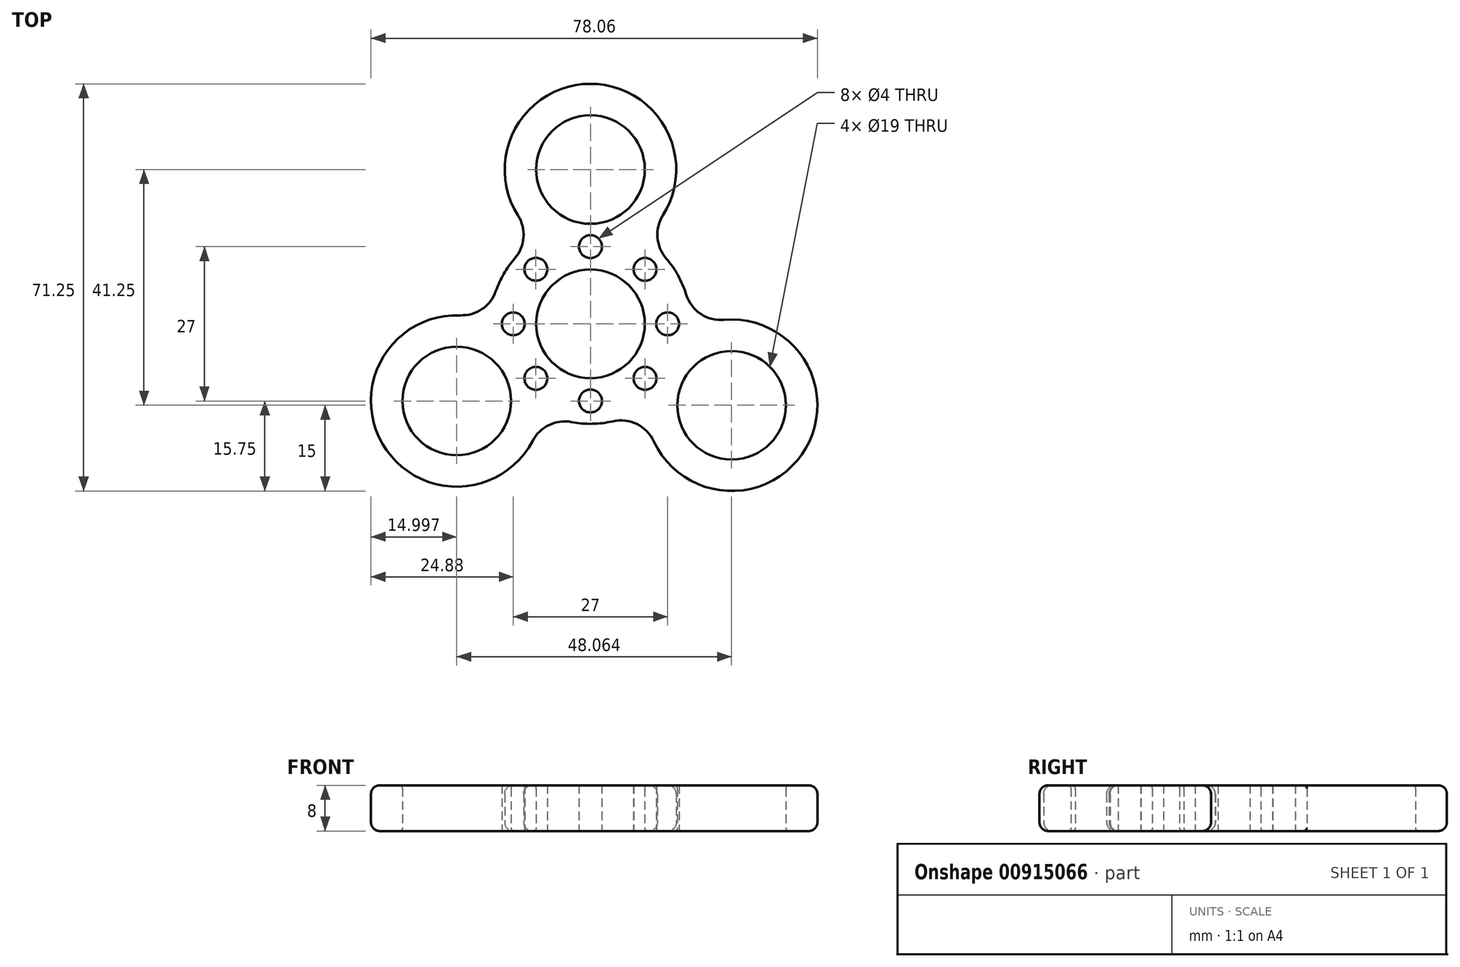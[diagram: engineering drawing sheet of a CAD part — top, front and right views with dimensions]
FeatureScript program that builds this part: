
annotation { "Feature Type Name" : "Feature", "Feature Type Description" : "" }
export const myFeature = defineFeature(function(context is Context, id is Id, definition is map)
    precondition{}
    {
        {
            var Q0;
            Q0=qCreatedBy(makeId("Top.planeOp"),FACE);
            var sketch = newSketch(context, id + "F0", { "sketchPlane" : qUnion([Q0])});
            skCircle(sketch, "E0", {"center": v(0, 0) * mm, "radius": 9.5 * mm});
            skArc(sketch, "E1", {"start": v(-13.24, 11.44) * mm, "mid": v(-15.16, 8.75) * mm, "end": v(-16.53, 5.75) * mm});
            skLineSegment(sketch, "E2", {"start": v(0, 9.5) * mm, "end": v(0, 12) * mm});
            skCircle(sketch, "E3", {"center": v(0, 27) * mm, "radius": 9.5 * mm});
            skCircle(sketch, "E4", {"center": v(-23.38, -13.5) * mm, "radius": 9.5 * mm});
            skArc(sketch, "E5", {"start": v(12.68, 18.99) * mm, "mid": v(0, 42) * mm, "end": v(-12.68, 18.99) * mm});
            skArc(sketch, "E6", {"start": v(-22.78, 1.49) * mm, "mid": v(-36.37, -21) * mm, "end": v(-10.1, -20.47) * mm});
            skCircle(sketch, "E7", {"center": v(24.68, -14.25) * mm, "radius": 9.5 * mm});
            skArc(sketch, "E8", {"start": v(11.08, -20.57) * mm, "mid": v(37.67, -21.75) * mm, "end": v(23.36, 0.7) * mm});
            skArc(sketch, "E9.trimOffspring", {"start": v(-3.29, -17.19) * mm, "mid": v(0.32, -17.5) * mm, "end": v(3.9, -17.06) * mm});
            skArc(sketch, "E10.trimOffspring", {"start": v(16.73, 5.15) * mm, "mid": v(15.31, 8.48) * mm, "end": v(13.24, 11.44) * mm});
            skPoint(sketch, "E11.visualSharp", {"position": v(17.47, -1.1) * mm});
            skArc(sketch, "E11.filletArc", {"start": v(16.73, 5.15) * mm, "mid": v(19.25, 1.75) * mm, "end": v(23.36, 0.7) * mm});
            skArc(sketch, "E12.filletArc", {"start": v(12.68, 18.99) * mm, "mid": v(11.71, 15.12) * mm, "end": v(13.24, 11.44) * mm});
            skPoint(sketch, "E13.visualSharp", {"position": v(-9, 15) * mm});
            skArc(sketch, "E13.filletArc", {"start": v(-13.24, 11.44) * mm, "mid": v(-11.71, 15.12) * mm, "end": v(-12.68, 18.99) * mm});
            skPoint(sketch, "E14.visualSharp", {"position": v(-17.5, 0.3) * mm});
            skArc(sketch, "E14.filletArc", {"start": v(-22.78, 1.49) * mm, "mid": v(-18.95, 2.58) * mm, "end": v(-16.53, 5.75) * mm});
            skPoint(sketch, "E15.visualSharp", {"position": v(-8.5, -15.3) * mm});
            skArc(sketch, "E15.filletArc", {"start": v(-3.29, -17.19) * mm, "mid": v(-7.24, -17.7) * mm, "end": v(-10.1, -20.47) * mm});
            skPoint(sketch, "E16.visualSharp", {"position": v(9.69, -14.58) * mm});
            skArc(sketch, "E16.filletArc", {"start": v(11.08, -20.57) * mm, "mid": v(8.11, -17.55) * mm, "end": v(3.9, -17.06) * mm});
            skCircle(sketch, "E17", {"center": v(0, 0) * mm, "radius": 13.5 * mm, "construction": true});
            skCircle(sketch, "E18", {"center": v(-13.5, 0) * mm, "radius": 2 * mm});
            skCircle(sketch, "E19", {"center": v(0, -13.5) * mm, "radius": 2 * mm});
            skCircle(sketch, "E20", {"center": v(13.5, 0) * mm, "radius": 2 * mm});
            skCircle(sketch, "E21", {"center": v(0, 13.5) * mm, "radius": 2 * mm});
            skCircle(sketch, "E22.1.0", {"center": v(0, 0) * mm, "radius": 13.5 * mm});
            skCircle(sketch, "E22.2.0", {"center": v(0, 0) * mm, "radius": 13.5 * mm});
            skLineSegment(sketch, "E23", {"start": v(0, 0) * mm, "end": v(9.53, 9.53) * mm, "construction": true});
            skLineSegment(sketch, "E24", {"start": v(0, 0) * mm, "end": v(0, 13.5) * mm, "construction": true});
            skLineSegment(sketch, "E25", {"start": v(0, 0) * mm, "end": v(-13.5, 0) * mm, "construction": true});
            skLineSegment(sketch, "E26", {"start": v(0, 0) * mm, "end": v(0, -13.5) * mm, "construction": true});
            skLineSegment(sketch, "E27", {"start": v(0, 0) * mm, "end": v(-9.55, 9.55) * mm, "construction": true});
            skLineSegment(sketch, "E28", {"start": v(0, 0) * mm, "end": v(-9.55, -9.55) * mm, "construction": true});
            skLineSegment(sketch, "E29", {"start": v(0, 0) * mm, "end": v(9.55, -9.55) * mm, "construction": true});
            skCircle(sketch, "E30", {"center": v(9.53, 9.53) * mm, "radius": 2 * mm});
            skCircle(sketch, "E31", {"center": v(-9.55, 9.55) * mm, "radius": 2 * mm});
            skCircle(sketch, "E32", {"center": v(-9.55, -9.55) * mm, "radius": 2 * mm});
            skCircle(sketch, "E33", {"center": v(9.55, -9.55) * mm, "radius": 2 * mm});
            skSolve(sketch);
        }
        {
            var Q0;
            Q0=makeQuery(id+"F0.imprint","IMPRINT",FACE,{"disambiguationData":[TD([[makeQuery(id+"F0.imprint","IMPRINT",EDGE,{"derivedFrom":sQuery(id+"F0.wireOp",EDGE,"E1")}),1.0]])]});
            var Q1;
            Q1=makeQuery(id+"F0.imprint","IMPRINT",FACE,{"disambiguationData":[TD([[makeQuery(id+"F0.imprint","IMPRINT",EDGE,{"derivedFrom":sQuery(id+"F0.wireOp",EDGE,"E0")}),-1.0]])]});
            extrude(context, id + "F1", {"entities" : qUnion([Q0, Q1]), "depth" : 8 * mm, "offsetDistance" : 25 * mm});
        }
        {
            var Q0;
            Q0=makeQuery(id+"F1.opExtrude","CAP_EDGE",EDGE,{"disambiguationData":[OSD([sQuery(id+"F0.wireOp",EDGE,"E6")])],"isStart":true});
            fillet(context, id + "F2", {"entities" : qUnion([Q0]), "radius" : 1.5 * mm, "tangentPropagation" : true, "allowEdgeOverflow" : false});
        }
        {
            var Q0;
            Q0=makeQuery(id+"F1.opExtrude","CAP_EDGE",EDGE,{"disambiguationData":[OSD([sQuery(id+"F0.wireOp",EDGE,"E5")])],"isStart":false});
            fillet(context, id + "F3", {"entities" : qUnion([Q0]), "radius" : 1.5 * mm, "tangentPropagation" : true, "allowEdgeOverflow" : false});
        }
        {
            var Q0;
            Q0=makeQuery(id+"F1.opExtrude","CAP_EDGE",EDGE,{"disambiguationData":[OSD([sQuery(id+"F0.wireOp",EDGE,"E4")])],"isStart":false});
            fillet(context, id + "F4", {"entities" : qUnion([Q0]), "radius" : 0.5 * mm, "tangentPropagation" : true, "allowEdgeOverflow" : false});
        }
        {
            var Q0;
            Q0=makeQuery(id+"F1.opExtrude","CAP_EDGE",EDGE,{"disambiguationData":[OSD([sQuery(id+"F0.wireOp",EDGE,"E3")])],"isStart":false});
            var Q1;
            Q1=makeQuery(id+"F1.opExtrude","CAP_EDGE",EDGE,{"disambiguationData":[OSD([sQuery(id+"F0.wireOp",EDGE,"E0")])],"isStart":false});
            var Q2;
            Q2=makeQuery(id+"F1.opExtrude","CAP_EDGE",EDGE,{"disambiguationData":[OSD([sQuery(id+"F0.wireOp",EDGE,"E7")])],"isStart":false});
            fillet(context, id + "F5", {"entities" : qUnion([Q0, Q1, Q2]), "radius" : 0.5 * mm, "tangentPropagation" : true, "allowEdgeOverflow" : false});
        }
        {
            var Q0;
            Q0=makeQuery(id+"F1.opExtrude","CAP_EDGE",EDGE,{"disambiguationData":[OSD([sQuery(id+"F0.wireOp",EDGE,"E4")])],"isStart":true});
            var Q1;
            Q1=makeQuery(id+"F1.opExtrude","CAP_EDGE",EDGE,{"disambiguationData":[OSD([sQuery(id+"F0.wireOp",EDGE,"E0")])],"isStart":true});
            var Q2;
            Q2=makeQuery(id+"F1.opExtrude","CAP_EDGE",EDGE,{"disambiguationData":[OSD([sQuery(id+"F0.wireOp",EDGE,"E3")])],"isStart":true});
            var Q3;
            Q3=makeQuery(id+"F1.opExtrude","CAP_EDGE",EDGE,{"disambiguationData":[OSD([sQuery(id+"F0.wireOp",EDGE,"E7")])],"isStart":true});
            fillet(context, id + "F6", {"entities" : qUnion([Q0, Q1, Q2, Q3]), "radius" : 0.5 * mm, "tangentPropagation" : true, "allowEdgeOverflow" : false});
        }
    });
